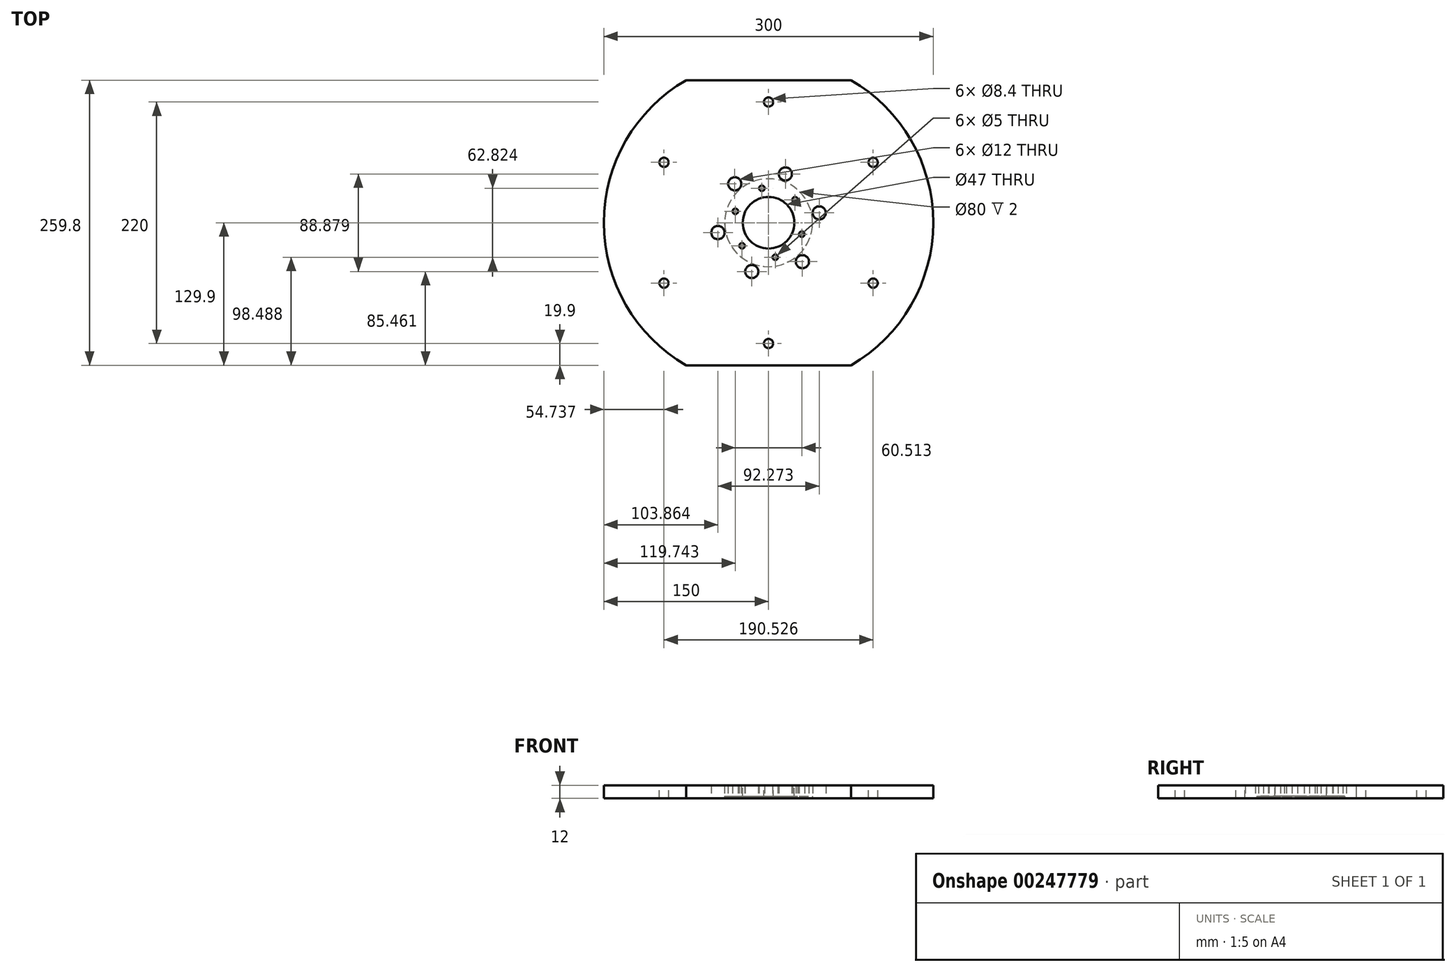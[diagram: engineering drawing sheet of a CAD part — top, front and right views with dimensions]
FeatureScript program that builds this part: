
annotation { "Feature Type Name" : "Feature", "Feature Type Description" : "" }
export const myFeature = defineFeature(function(context is Context, id is Id, definition is map)
    precondition{}
    {
        {
            var Q0;
            Q0=qCreatedBy(makeId("Top.planeOp"),FACE);
            var sketch = newSketch(context, id + "F0", { "sketchPlane" : qUnion([Q0])});
            skArc(sketch, "E0.cCircle", {"start": v(-75, 129.9) * mm, "mid": v(-150, 0) * mm, "end": v(-75, -129.9) * mm});
            skLineSegment(sketch, "E0.1", {"start": v(-75, 129.9) * mm, "end": v(75, 129.9) * mm});
            skLineSegment(sketch, "E0.4", {"start": v(75, -129.9) * mm, "end": v(-75, -129.9) * mm});
            skArc(sketch, "E1.trimOffspring", {"start": v(75, -129.9) * mm, "mid": v(150, 0) * mm, "end": v(75, 129.9) * mm});
            skPoint(sketch, "E0.5.end.orphan", {"position": v(-150, 0) * mm});
            skCircle(sketch, "E2", {"center": v(0, 0) * mm, "radius": 110 * mm, "construction": true});
            skCircle(sketch, "E3", {"center": v(0, 110) * mm, "radius": 4.2 * mm});
            skCircle(sketch, "E4.1.0", {"center": v(-95.26, 55) * mm, "radius": 4.2 * mm});
            skCircle(sketch, "E4.2.0", {"center": v(-95.26, -55) * mm, "radius": 4.2 * mm});
            skCircle(sketch, "E4.3.0", {"center": v(0, -110) * mm, "radius": 4.2 * mm});
            skCircle(sketch, "E4.4.0", {"center": v(95.26, -55) * mm, "radius": 4.2 * mm});
            skCircle(sketch, "E4.5.0", {"center": v(95.26, 55) * mm, "radius": 4.2 * mm});
            skCircle(sketch, "E5", {"center": v(0, 0) * mm, "radius": 23.5 * mm});
            skSolve(sketch);
        }
        {
            var Q0;
            Q0=makeQuery(id+"F0.imprint","IMPRINT",FACE,{"disambiguationData":[TD([[makeQuery(id+"F0.imprint","IMPRINT",EDGE,{"derivedFrom":sQuery(id+"F0.wireOp",EDGE,"E0.cCircle")}),1.0]])]});
            extrude(context, id + "F1", {"entities" : qUnion([Q0]), "oppositeDirection" : true, "depth" : 12 * mm});
        }
        {
            var Q0;
            Q0=makeQuery(id+"F1.opExtrude","CAP_FACE",FACE,{"disambiguationData":[OSD([sQuery(id+"F0.wireOp",EDGE,"E0.cCircle"),sQuery(id+"F0.wireOp",EDGE,"E0.1"),sQuery(id+"F0.wireOp",EDGE,"E0.4"),sQuery(id+"F0.wireOp",EDGE,"E1.trimOffspring"),sQuery(id+"F0.wireOp",EDGE,"E3"),sQuery(id+"F0.wireOp",EDGE,"E4.1.0"),sQuery(id+"F0.wireOp",EDGE,"E4.2.0"),sQuery(id+"F0.wireOp",EDGE,"E4.3.0"),sQuery(id+"F0.wireOp",EDGE,"E4.4.0"),sQuery(id+"F0.wireOp",EDGE,"E4.5.0"),sQuery(id+"F0.wireOp",EDGE,"E5")])],"isStart":false});
            cPlane(context, id + "F2", {"entities" : qUnion([Q0]), "cplaneType" : CPlaneType.OFFSET, "offset" : 0 * mm, "width" : 150 * mm, "height" : 150 * mm});
        }
        {
            var Q0;
            Q0=qCreatedBy(id+"F2.planeOp",FACE);
            var sketch = newSketch(context, id + "F3", { "sketchPlane" : qUnion([Q0])});
            skCircle(sketch, "E6", {"center": v(0, 0) * mm, "radius": 40 * mm});
            skSolve(sketch);
        }
        {
            var Q0;
            Q0=qSketchRegion(id+"F3",true);
            extrude(context, id + "F4", {"entities" : qUnion([Q0]), "operationType" : NewBodyOperationType.REMOVE, "oppositeDirection" : true, "depth" : 2 * mm, "hasSecondDirection" : true, "secondDirectionOppositeDirection" : false, "secondDirectionDepth" : 10 * mm});
        }
        {
            var Q0;
            Q0=qCreatedBy(id+"F2.planeOp",FACE);
            var sketch = newSketch(context, id + "F5", { "sketchPlane" : qUnion([Q0])});
            skCircle(sketch, "E7", {"center": v(0, 0) * mm, "radius": 32 * mm, "construction": true});
            skLineSegment(sketch, "E8", {"start": v(0, 0) * mm, "end": v(8.68, 44.64) * mm, "construction": true});
            skPoint(sketch, "E9", {"position": v(6.1, 31.41) * mm});
            skPoint(sketch, "E10.1.0", {"position": v(-24.15, 21) * mm});
            skPoint(sketch, "E10.2.0", {"position": v(-30.26, -10.42) * mm});
            skPoint(sketch, "E10.3.0", {"position": v(-6.1, -31.41) * mm});
            skPoint(sketch, "E10.4.0", {"position": v(24.15, -21) * mm});
            skPoint(sketch, "E10.5.0", {"position": v(30.26, 10.42) * mm});
            skCircle(sketch, "E11", {"center": v(0, 0) * mm, "radius": 55 * mm, "construction": true});
            skCircle(sketch, "E12", {"center": v(0, 0) * mm, "radius": 47 * mm, "construction": true});
            skLineSegment(sketch, "E13", {"start": v(0, 0) * mm, "end": v(-26.12, 75.86) * mm, "construction": true});
            skPoint(sketch, "E14", {"position": v(-15.3, 44.44) * mm});
            skPoint(sketch, "E15.1.0", {"position": v(-46.14, 8.97) * mm});
            skPoint(sketch, "E15.2.0", {"position": v(-30.83, -35.47) * mm});
            skPoint(sketch, "E15.3.0", {"position": v(15.3, -44.44) * mm});
            skPoint(sketch, "E15.4.0", {"position": v(46.14, -8.97) * mm});
            skPoint(sketch, "E15.5.0", {"position": v(30.83, 35.47) * mm});
            skSolve(sketch);
        }
        {
            var Q0;
            Q0=sQuery(id+"F5.wireOp",VERTEX,"E9");
            var Q1;
            Q1=sQuery(id+"F5.wireOp",VERTEX,"E10.1.0");
            var Q2;
            Q2=sQuery(id+"F5.wireOp",VERTEX,"E10.2.0");
            var Q3;
            Q3=sQuery(id+"F5.wireOp",VERTEX,"E10.3.0");
            var Q4;
            Q4=sQuery(id+"F5.wireOp",VERTEX,"E10.4.0");
            var Q5;
            Q5=sQuery(id+"F5.wireOp",VERTEX,"E10.5.0");
            var Q6;
            Q6=makeQuery(id+"F1.opExtrude","SWEPT_BODY",BODY,{"disambiguationData":[OSD([sQuery(id+"F0.wireOp",EDGE,"E0.cCircle"),sQuery(id+"F0.wireOp",EDGE,"E0.1"),sQuery(id+"F0.wireOp",EDGE,"E0.4"),sQuery(id+"F0.wireOp",EDGE,"E1.trimOffspring"),sQuery(id+"F0.wireOp",EDGE,"E3"),sQuery(id+"F0.wireOp",EDGE,"E4.1.0"),sQuery(id+"F0.wireOp",EDGE,"E4.2.0"),sQuery(id+"F0.wireOp",EDGE,"E4.3.0"),sQuery(id+"F0.wireOp",EDGE,"E4.4.0"),sQuery(id+"F0.wireOp",EDGE,"E4.5.0"),sQuery(id+"F0.wireOp",EDGE,"E5")])]});
            hole(context, id + "F6", {"style" : HoleStyle.SIMPLE, "endStyle" : HoleEndStyle.THROUGH, "holeDiameter" : 5 * mm, "locations" : qUnion([Q0, Q1, Q2, Q3, Q4, Q5]), "scope" : qUnion([Q6]), "isTappedThrough" : true});
        }
        {
            var Q0;
            Q0=sQuery(id+"F5.wireOp",VERTEX,"E15.2.0");
            var Q1;
            Q1=sQuery(id+"F5.wireOp",VERTEX,"E15.3.0");
            var Q2;
            Q2=sQuery(id+"F5.wireOp",VERTEX,"E15.4.0");
            var Q3;
            Q3=sQuery(id+"F5.wireOp",VERTEX,"E15.5.0");
            var Q4;
            Q4=sQuery(id+"F5.wireOp",VERTEX,"E14");
            var Q5;
            Q5=sQuery(id+"F5.wireOp",VERTEX,"E15.1.0");
            var Q6;
            Q6=makeQuery(id+"F1.opExtrude","SWEPT_BODY",BODY,{"disambiguationData":[OSD([sQuery(id+"F0.wireOp",EDGE,"E0.cCircle"),sQuery(id+"F0.wireOp",EDGE,"E0.1"),sQuery(id+"F0.wireOp",EDGE,"E0.4"),sQuery(id+"F0.wireOp",EDGE,"E1.trimOffspring"),sQuery(id+"F0.wireOp",EDGE,"E3"),sQuery(id+"F0.wireOp",EDGE,"E4.1.0"),sQuery(id+"F0.wireOp",EDGE,"E4.2.0"),sQuery(id+"F0.wireOp",EDGE,"E4.3.0"),sQuery(id+"F0.wireOp",EDGE,"E4.4.0"),sQuery(id+"F0.wireOp",EDGE,"E4.5.0"),sQuery(id+"F0.wireOp",EDGE,"E5")])]});
            hole(context, id + "F7", {"style" : HoleStyle.SIMPLE, "endStyle" : HoleEndStyle.THROUGH, "holeDiameter" : 12 * mm, "locations" : qUnion([Q0, Q1, Q2, Q3, Q4, Q5]), "scope" : qUnion([Q6]), "isTappedThrough" : true});
        }
    });
